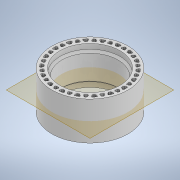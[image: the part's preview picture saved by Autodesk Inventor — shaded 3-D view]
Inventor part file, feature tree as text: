
AUTODESK INVENTOR PART (.ipt)
format: ipt  version: 2020 (Build 240168000, 168)  size: 429,056 bytes
history: native  units: mm
features: extrude x4, sketch x4, fillet x2, pattern_circular x2, plane x1, chamfer x1
ambient origin geometry x8: Origin, YZ Plane, XZ Plane, XY Plane, X Axis, Y Axis, Z Axis, Center Point
bodies: Solid1 (feature_tree)
feature tree (14):
  extrude  "Extrusion1"  Depth=30.0mm
  plane  "Work Plane1"
  extrude  "Extrusion2"  [1 undecoded]
  chamfer  "Chamfer1"  Distance=1.0mm Angle=45.0deg
  extrude  "Extrusion3"  TaperAngle=30.0deg  [1 undecoded]
  fillet  "Fillet1"  [1 undecoded]
  pattern_circular  "Circular Pattern1"  [2 undecoded]
  extrude  "Extrusion4"  Depth=1.107726mm
  fillet  "Fillet2"  Radius=1.0mm
  pattern_circular  "Circular Pattern2"  [2 undecoded]
  sketch  "Sketch1"  dims[d0=38.0mm d1=30.0mm]
  sketch  "Sketch2"  dims[d2=19.0mm d3=0.0mm d4=-9.5mm]
  sketch  "Sketch3"  dims[d5=28.0mm]
  sketch  "Sketch4"  dims[d6=7.0mm d7=7.0mm d8=0.0mm d9=0.0mm d10=1.0mm d11=2.0mm d12=45.0deg d15=30.0deg d16=30.0deg d17=1.2mm d18=1.2mm d19=1.0mm d20=0.5mm d21=0.0mm d22=19.0mm d23=0.0mm d24=0.4mm d25=180.0mm d26=360.0deg d28=0.5mm d29=1.2mm d30=1.2mm d31=0.5mm d34=1.745329mm d35=19.0mm d36=0.0mm d37=0.4mm d38=1.107726mm d39=1.107726mm d40=180.0mm d41=360.0deg]
note: 7 required parameter values undecoded (feature->parameter linkage not recoverable at this tier; creation-order binding heuristic only, values carry confidence <= 0.55)
